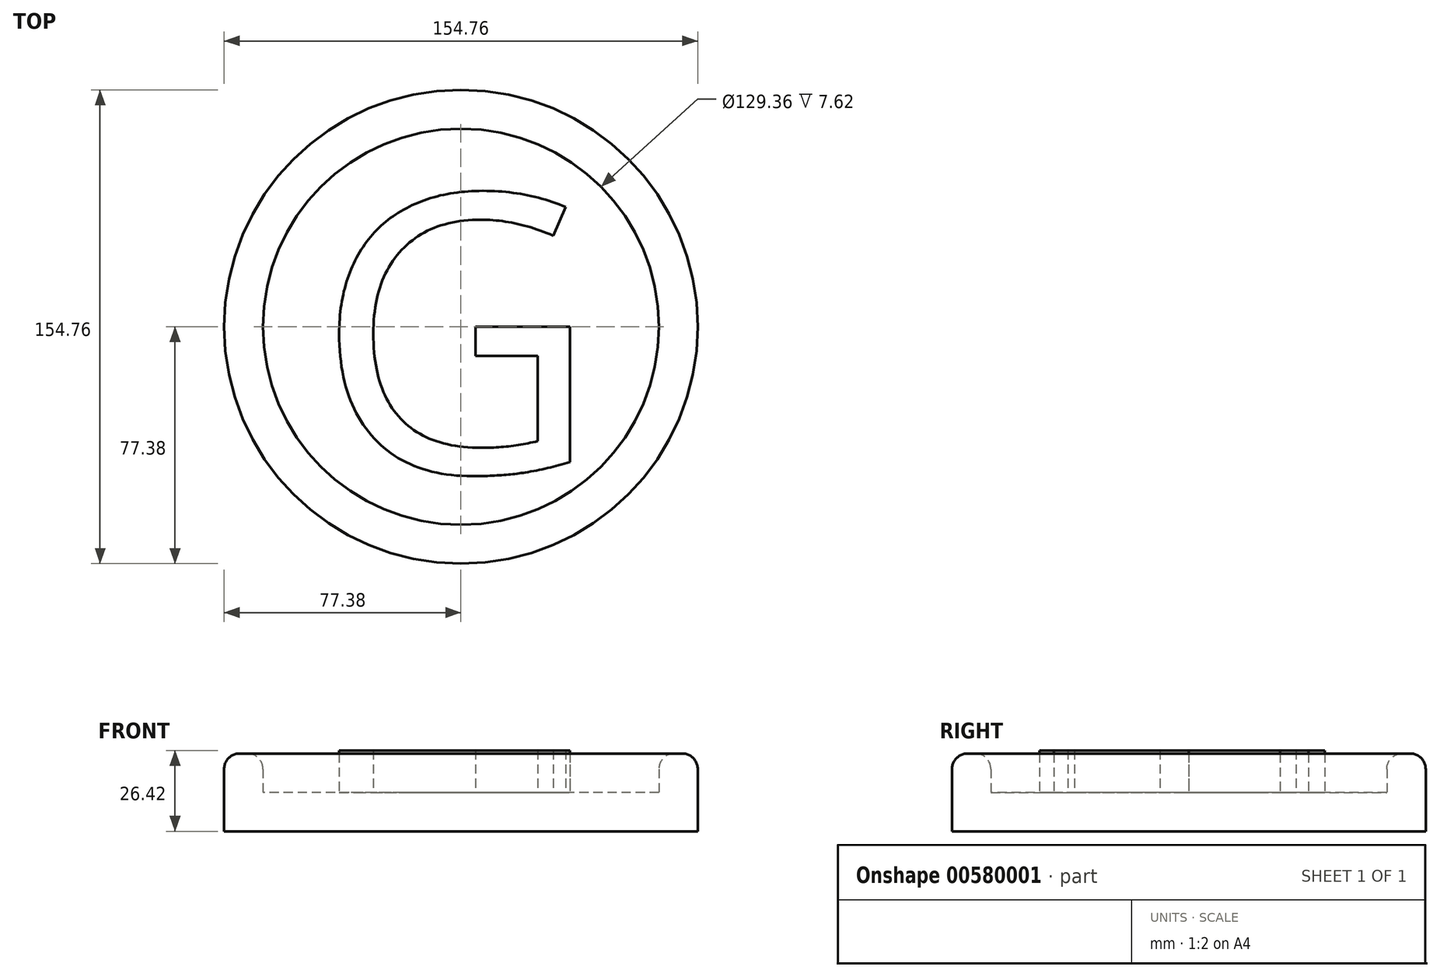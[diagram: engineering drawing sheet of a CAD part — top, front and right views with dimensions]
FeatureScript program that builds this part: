
annotation { "Feature Type Name" : "Feature", "Feature Type Description" : "" }
export const myFeature = defineFeature(function(context is Context, id is Id, definition is map)
    precondition{}
    {
        {
            var Q0;
            Q0=qCreatedBy(makeId("Top.planeOp"),FACE);
            var sketch = newSketch(context, id + "F0", { "sketchPlane" : qUnion([Q0])});
            skCircle(sketch, "E0", {"center": v(0, 0) * mm, "radius": 77.38 * mm});
            skSolve(sketch);
        }
        {
            var Q0;
            Q0=makeQuery(id+"F0.imprint","IMPRINT",FACE,{"disambiguationData":[TD([[makeQuery(id+"F0.imprint","IMPRINT",EDGE,{"derivedFrom":sQuery(id+"F0.wireOp",EDGE,"E0")}),1.0]])]});
            extrude(context, id + "F1", {"entities" : qUnion([Q0]), "depth" : 25.4 * mm, "offsetDistance" : 25.4 * mm});
        }
        {
            var Q0;
            Q0=makeQuery(id+"F1.opExtrude","CAP_FACE",FACE,{"disambiguationData":[OSD([sQuery(id+"F0.wireOp",EDGE,"E0")])],"isStart":false});
            shell(context, id + "F2", {"entities" : qUnion([Q0]), "thickness" : 12.7 * mm});
        }
        {
            var Q0;
            Q0=makeQuery(id+"F1.opExtrude","CAP_FACE",FACE,{"disambiguationData":[OSD([sQuery(id+"F0.wireOp",EDGE,"E0")])],"isStart":false});
            fillet(context, id + "F3", {"entities" : qUnion([Q0]), "radius" : 5.08 * mm, "tangentPropagation" : true, "allowEdgeOverflow" : false});
        }
        {
            var Q0;
            {var subQ0=sQuery(id+"F0.wireOp",EDGE,"E0");Q0=makeQuery(id+"F2.opShell","OFFSET_FACE",FACE,{"disambiguationData":[OSD([subQ0]),TDD([makeQuery(id+"F1.opExtrude","CAP_FACE",FACE,{"disambiguationData":[OSD([subQ0])],"isStart":true})])]});}
            var sketch = newSketch(context, id + "F4", { "sketchPlane" : qUnion([Q0])});
            skText(sketch, "E1", { "text": "G", "fontName": "OpenSans-Regular.ttf"});
            const initialGuessF4  = {"E1": [-0.04753, -0.04755, 1, 0, 0.09142]};
            skSetInitialGuess(sketch, initialGuessF4);
            skSolve(sketch);
        }
        {
            var Q0;
            Q0=makeQuery(id+"F4.imprint","IMPRINT",FACE,{"disambiguationData":[TD([[makeQuery(id+"F4.imprint","IMPRINT",EDGE,{"derivedFrom":sQuery(id+"F4.wireOp",EDGE,"E1.sketch_text.stroke-0")}),-1.0]])]});
            extrude(context, id + "F5", {"entities" : qUnion([Q0]), "operationType" : NewBodyOperationType.ADD, "depth" : 13.72 * mm, "offsetDistance" : 25.4 * mm});
        }
    });
